# Revit family: HC_Boiler_Condensate Flow_MEPcontent_Remeha_Gas 320 Ace 5-7_Right_GB-EN
name_source: partatom
category: Mechanical Equipment
revit_build: Autodesk Revit 2018 (Build: 20170223_1515(x64)
units: mm (PartAtom-declared; Revit-internal decimal feet)

## family parameters
Always vertical = Yes
Classification = None
Cut with Voids When Loaded = No
OmniClass Number = 23.75.10.11.14
OmniClass Title = Hot Water Heat Generators
Part Type = Normal
Room Calculation Point = No
Round Connector Dimension = Use Diameter
Shared = No
Work Plane-Based = No

## types (3) — shared parameters
6 Monthly = 06-02
Access Clearance Front = 800 mm  [stored 2.62467 ft]
Access Clearance Left = 800 mm  [stored 2.62467 ft]
Access Clearance Rear = 300 mm  [stored 0.984252 ft]
Access Clearance Right = 150 mm  [stored 0.492126 ft]
Access Clearance Top = 450 mm  [stored 1.47638 ft]
Air Inlet Connection Size = 250 mm  [stored 0.82021 ft]
Annually = 06-02
BMS Links = Yes
Base Family Version = 12.23
Blue = Color RGB 075-186-252
Burner Control Type = Modulating
CE Approval = PIN 0063CU3937
Colour = RAL 7016 , RAL 2002
Condensate Drain Size = 32 mm  [stored 0.104987 ft]
Condensate Drain Type = Plain
Configuration = Single boiler
Content Supplier URL = www.MEPcontent.com
Control Type = R-Bus,0 - 10V, Open Therm, Volt free enable, Direct boiler weather compensating control systems available from Remeha as optional extra's.
Custom = No
Daily = 0
Drain Connection Size = 15 mm  [stored 0.0492126 ft]
Drain Connection Type = Threaded
EMCS Version = 4.0
ETIM Article Class = EC010232
ErP Energy Label = 0
ErP Seasonal Efficiency = 0 %
Expected Life = 15
External Material = Steel
Family Version = 12.17
Finish = High Polish Gardner 60 GRAD 91EH
Flow and Return Connection Size = 80 mm  [stored 0.262467 ft]
Flow and Return Connection Type = Flanged
Flue Connection Size = 250 mm  [stored 0.82021 ft]
Flue or Air Intake Classification = B23, B23p, C33, C53, C63 and C93
Frequency = 50 Hz
Fuel Connection Size = 50 mm  [stored 0.164042 ft]
Fuel Connection Type = Threaded
Full Load Current = 0 A
Fuse Rating = 10 A
GLN = 8713809000004
Glass = Color RGB 218-227-224
Grey = Color RAL 7016
Heat Exchanger Material = Aluminium
Heater Operation = Condensing
Hydraulic Resistance at 11C temperature differential = 0.4
Hydraulic Resistance at 20C temperature differential = 0.1
IFCExportAs = IfcBoiler
IFCExportType = NOTDEFINED
IP Rating = X1
Interlocks = Yes
Logo = Color RGB 126-126-126
MEPcontent Class = BOILER_CONDENSATE_FLOW
Manufacturer = Remeha
Manufacturer URL = https://www.remeha.co.uk
Manufacturer Website = https://www.remeha.co.uk
Maximum Gas Inlet Pressure = 0.0 bar
Maximum Oil Inlet Pressure = 0.0 bar
Maximum Operating Pressure = 7.0 bar
Minimum Gas Inlet Pressure = 0.0 bar
Minimum Oil Inlet Pressure = 0.0 bar
Minimum Operating Pressure = 0.8 bar
Monthly = 0
Mounting = Floor Standing
Nominal Gas Inlet Pressure = 0.0 bar
Nominal Oil Inlet Pressure = 0.0 bar
O&M Manual = https://www.remeha.co.uk
Optional Fuel = No Optional Fuel
Overall Height = 1550 mm  [stored 5.0853 ft]
Overall Length = 1862 mm  [stored 6.10892 ft]
Overall Width = 707 mm  [stored 2.31955 ft]
Phase = 1
Pipe Type Category = M561
Primary Fuel = Gas - NG
Product Line = Gas 320 Ace
Product Literature = https://www.remeha.co.uk
Quarterly = 0
Rated Criteria = 80/60
Red = Color RAL 2002
Reference Standard = EN 15502-1
Revit Version = 2018
Safety Valve Connection Size = 40 mm  [stored 0.131234 ft]
Safety Valve Connection Type = Threaded
Safety Valve Diameter = 65 mm  [stored 0.213255 ft]
Shape = Rectangular (Horizontal)
Starting Current = 0 A
Supply Phase = 1
Turndown Ratio = 5:1
Type = Space heating
URL = https://mep.trimble.com
Use Nominal Diameter = Yes
Voltage = 230 V
Water Treatment Required = Yes
Weekly = 0
White = Color RGB 255-255-255
Yellow = Color RGB 255-255-000
zero-valued in all types: Access Clearance Bottom, Life Cycle Analysis, Oil Consumption rate

## per-type parameters (varying)
| type | Article Description | Building Regulations Seasonal Efficiency | Description | ErP Rated Efficiency at Full Load | ErP Rated Efficiency at Part Load | Features | Gas Consumption rate | Gross Weight | Maximum Power Consumption | Minimum Flow Rate at 11C temperature differential | Minimum Flow Rate at 20C temperature differential | Minimum Power Consumption | NOx Emissions - 2 BREEAM Credits | NOx Emissions - Standard | Product Model Number | Product Range | Rated Output | Shipping Weight | Sound Pressure Level | Type Formula | Water Content |
| 285 | FSB GAS 320 285kW | 96.46 % | FSB GAS 320 285kW | 88.29 % | 98.38 % | Remeha's Gas 320 Ace 285 range are compact high efficiency floor standing gas condensing boilers. Ideally suited for single or multiple cascade arrangments for new and refurbishment projects | 28.1 m3/h | 415.00 kg | 280 W | 5.6 L/s | 3.1 L/s | 52 W | 15 mg/kWh | 43 mg/kWh | 7752866-01 | Gas 320 Ace - 285 - 5 section | 261 W | 436.00 kg | 61.2 dBA | 285 mm  [stored 0.935039 ft] | 49.0 L |
| 355 | FSB GAS 320 355kW | 96.33 % | FSB GAS 320 355kW | 88.38 % | 98.2 % | Remeha's Gas 320 Ace 355 range are compact high efficiency floor standing gas condensing boilers. Ideally suited for single or multiple cascade arrangments for new and refurbishment projects | 35.2 m3/h | 460.00 kg | 345 W | 7.0 L/s | 3.9 L/s | 57 W | 16 mg/kWh | 43 mg/kWh | 7752867-01 | Gas 320 Ace - 355 - 6 section | 327 W | 470.00 kg | 61.2 dBA | 355 mm | 60.0 L |
| 430 | FSB GAS 320 430kW | 96.2 % | FSB GAS 320 430kW | 88.47 % | 98.02 % | Remeha's Gas 320 Ace 430 range are compact high efficiency floor standing gas condensing boilers. Ideally suited for single or multiple cascade arrangments for new and refurbishment projects | 42.5 m3/h | 506.00 kg | 450 W | 8.5 L/s | 4.7 L/s | 64 W | 16 mg/kWh | 44 mg/kWh | 7752868-01 | Gas 320 Ace - 430 - 7 section | 395 W | 505.00 kg | 64.8 dBA | 430 mm | 71.0 L |

note: column(s) folded — value = type name in every type: Article Type, Model

note: source unit labels omitted for Hydraulic Resistance at 11C temperature differential, Hydraulic Resistance at 20C temperature differential — the stored unit's dimension contradicts the parameter name (converter mislabeling)

note: [stored X ft] marks values corroborated as IEEE doubles in the binary element streams (Revit-internal decimal feet)

## geometry (parser evidence)
native form markers: Sweep x11
no freeform markers — native parametric forms only
